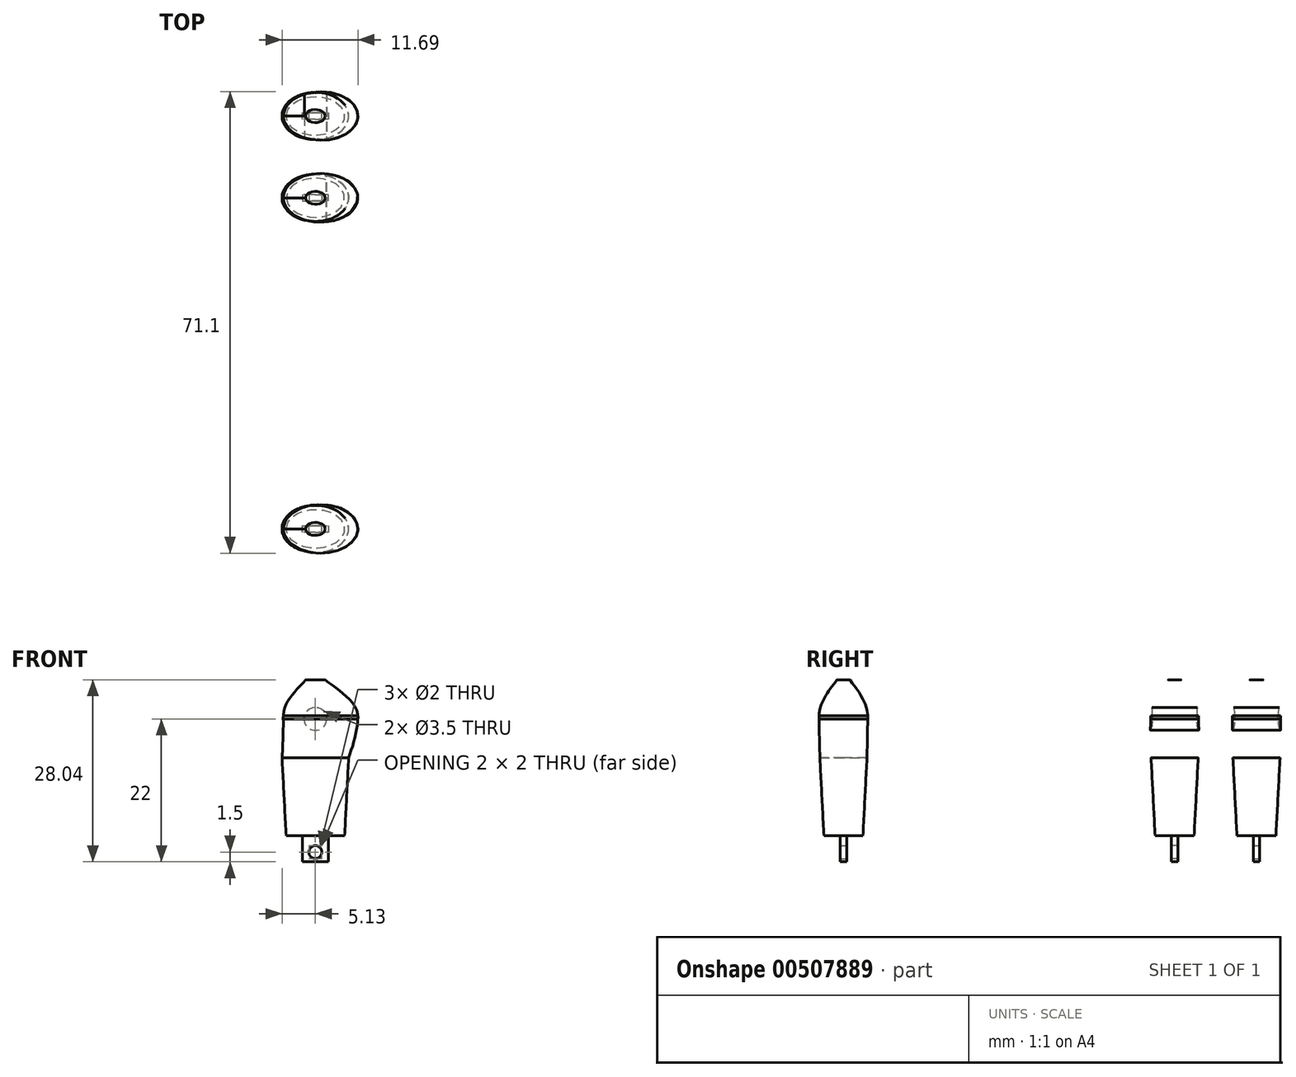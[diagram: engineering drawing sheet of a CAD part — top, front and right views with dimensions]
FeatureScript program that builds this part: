
annotation { "Feature Type Name" : "Feature", "Feature Type Description" : "" }
export const myFeature = defineFeature(function(context is Context, id is Id, definition is map)
    precondition{}
    {
        {
            var Q0;
            Q0=qCreatedBy(makeId("Top.planeOp"),FACE);
            var sketch = newSketch(context, id + "F0", { "sketchPlane" : qUnion([Q0])});
            skEllipse(sketch, "E0", {"center": v(0, 0) * mm, "majorRadius": 4.5 * mm, "minorRadius": 3 * mm, "majorAxis": v(1, 0)});
            skSolve(sketch);
        }
        {
            var Q0;
            Q0=makeQuery(id+"F0.imprint","IMPRINT",FACE,{"disambiguationData":[TD([[makeQuery(id+"F0.imprint","IMPRINT",EDGE,{"derivedFrom":sQuery(id+"F0.wireOp",EDGE,"E0")}),1.0]])]});
            var Q1;
            Q1=sQuery(id+"F0.wireOp",EDGE,"E0");
            extrude(context, id + "F1", {"entities" : qUnion([Q0]), "surfaceEntities" : qUnion([Q1]), "depth" : 12 * mm, "offsetDistance" : 25 * mm, "hasDraft" : true, "draftAngle" : 3 * degree});
        }
        {
            var Q0;
            Q0=makeQuery(id+"F1.opExtrude","CAP_FACE",FACE,{"disambiguationData":[OSD([sQuery(id+"F0.wireOp",EDGE,"E0")])],"isStart":false});
            cPlane(context, id + "F2", {"entities" : qUnion([Q0]), "cplaneType" : CPlaneType.OFFSET, "offset" : 6.5 * mm, "width" : 150 * mm, "height" : 150 * mm});
        }
        {
            var Q0;
            Q0=qCreatedBy(id+"F2.planeOp",FACE);
            var sketch = newSketch(context, id + "F3", { "sketchPlane" : qUnion([Q0])});
            skEllipse(sketch, "E1", {"center": v(0, 0) * mm, "majorRadius": 5.75 * mm, "minorRadius": 3.75 * mm, "majorAxis": v(1, 0)});
            skSolve(sketch);
        }
        {
            var Q0;
            Q0=makeQuery(id+"F3.imprint","IMPRINT",FACE,{"disambiguationData":[TD([[makeQuery(id+"F3.imprint","IMPRINT",EDGE,{"derivedFrom":sQuery(id+"F3.wireOp",EDGE,"E1")}),1.0]])]});
            var Q1;
            Q1=sQuery(id+"F3.wireOp",EDGE,"E1");
            extrude(context, id + "F4", {"entities" : qUnion([Q0]), "surfaceEntities" : qUnion([Q1]), "oppositeDirection" : true, "depth" : .5 * mm, "offsetDistance" : 25 * mm});
        }
        {
            var Q0;
            Q0=makeQuery(id+"F4.opExtrude","SWEPT_BODY",BODY,{"disambiguationData":[OSD([sQuery(id+"F3.wireOp",EDGE,"E1")])]});
            transform(context, id + "F5", {"entities" : qUnion([Q0]), "transformType" : TransformType.TRANSLATION_3D, "dx" : 0.8 * mm, "dy" : 0 * mm, "dz" : 0 * mm, "makeCopy" : false});
        }
        {
            var Q0;
            Q0=makeQuery(id+"F4.opExtrude","CAP_FACE",FACE,{"disambiguationData":[OSD([sQuery(id+"F3.wireOp",EDGE,"E1")])],"isStart":true});
            cPlane(context, id + "F6", {"entities" : qUnion([Q0]), "cplaneType" : CPlaneType.OFFSET, "offset" : 5.5 * mm, "width" : 150 * mm, "height" : 150 * mm});
        }
        {
            var Q0;
            Q0=qCreatedBy(id+"F6.planeOp",FACE);
            var sketch = newSketch(context, id + "F7", { "sketchPlane" : qUnion([Q0])});
            skEllipse(sketch, "E2", {"center": v(0, 0) * mm, "majorRadius": 1.5 * mm, "minorRadius": 1 * mm, "majorAxis": v(1, 0)});
            skSolve(sketch);
        }
        {
            var Q0;
            Q0=makeQuery(id+"F7.imprint","IMPRINT",FACE,{"disambiguationData":[TD([[makeQuery(id+"F7.imprint","IMPRINT",EDGE,{"derivedFrom":sQuery(id+"F7.wireOp",EDGE,"E2")}),1.0]])]});
            var Q1;
            Q1=sQuery(id+"F7.wireOp",EDGE,"E2");
            extrude(context, id + "F8", {"entities" : qUnion([Q0]), "surfaceEntities" : qUnion([Q1]), "depth" : 0.04 * mm, "offsetDistance" : 25 * mm});
        }
        {
            var Q0;
            Q0=makeQuery(id+"F1.opExtrude","CAP_FACE",FACE,{"disambiguationData":[OSD([sQuery(id+"F0.wireOp",EDGE,"E0")])],"isStart":false});
            var Q1;
            Q1=makeQuery(id+"F4.opExtrude","CAP_FACE",FACE,{"disambiguationData":[OSD([sQuery(id+"F3.wireOp",EDGE,"E1")])],"isStart":false});
            var Q2;
            Q2=makeQuery(id+"F4.opExtrude","CAP_FACE",FACE,{"disambiguationData":[OSD([sQuery(id+"F3.wireOp",EDGE,"E1")])],"isStart":true});
            var Q3;
            Q3=makeQuery(id+"F8.opExtrude","CAP_FACE",FACE,{"disambiguationData":[OSD([sQuery(id+"F7.wireOp",EDGE,"E2")])],"isStart":true});
            loft(context, id + "F9", {"sheetProfilesArray" : [{ "sheetProfileEntities" : qUnion([Q0]) }, { "sheetProfileEntities" : qUnion([Q1]) }, { "sheetProfileEntities" : qUnion([Q2]) }, { "sheetProfileEntities" : qUnion([Q3]) }]});
        }
        {
            var Q0;
            Q0=makeQuery(id+"F1.opExtrude","CAP_FACE",FACE,{"disambiguationData":[OSD([sQuery(id+"F0.wireOp",EDGE,"E0")])],"isStart":true});
            var sketch = newSketch(context, id + "F10", { "sketchPlane" : qUnion([Q0])});
            skLineSegment(sketch, "E3", {"start": v(-2, 0) * mm, "end": v(-2, 0.5) * mm});
            skLineSegment(sketch, "E4", {"start": v(-2, 0.5) * mm, "end": v(2, 0.5) * mm});
            skLineSegment(sketch, "E5", {"start": v(2, 0.5) * mm, "end": v(2, 0) * mm});
            skLineSegment(sketch, "E6", {"start": v(2, 0) * mm, "end": v(2, -0.5) * mm});
            skLineSegment(sketch, "E7", {"start": v(2, -0.5) * mm, "end": v(-2, -0.5) * mm});
            skLineSegment(sketch, "E8", {"start": v(-2, -0.5) * mm, "end": v(-2, 0) * mm});
            skLineSegment(sketch, "E9", {"start": v(0, 0) * mm, "end": v(-2, 0) * mm, "construction": true});
            skSolve(sketch);
        }
        {
            var Q0;
            Q0=makeQuery(id+"F10.imprint","IMPRINT",FACE,{"disambiguationData":[TD([[makeQuery(id+"F10.imprint","IMPRINT",EDGE,{"derivedFrom":sQuery(id+"F10.wireOp",EDGE,"E3")}),-1.0]])]});
            extrude(context, id + "F11", {"entities" : qUnion([Q0]), "operationType" : NewBodyOperationType.ADD, "depth" : 4 * mm, "offsetDistance" : 25 * mm});
        }
        {
            var Q0;
            Q0=makeQuery(id+"F11.opExtrude","SWEPT_FACE",FACE,{"disambiguationData":[OSD([sQuery(id+"F10.wireOp",EDGE,"E4")])]});
            var sketch = newSketch(context, id + "F12", { "sketchPlane" : qUnion([Q0])});
            skLineSegment(sketch, "E10", {"start": v(0, 0) * mm, "end": v(0, -2.5) * mm, "construction": true});
            skPoint(sketch, "E10.endSnap0", {"position": v(0, -4) * mm});
            skCircle(sketch, "E11", {"center": v(0, -2.5) * mm, "radius": 1 * mm});
            skSolve(sketch);
        }
        {
            var Q0;
            Q0=makeQuery(id+"F12.imprint","IMPRINT",FACE,{"disambiguationData":[TD([[makeQuery(id+"F12.imprint","IMPRINT",EDGE,{"derivedFrom":sQuery(id+"F12.wireOp",EDGE,"E11")}),1.0]])]});
            var Q1;
            Q1=sQuery(id+"F12.wireOp",EDGE,"E11");
            var Q2;
            Q2=makeQuery(id+"F11.opExtrude","SWEPT_FACE",FACE,{"disambiguationData":[OSD([sQuery(id+"F10.wireOp",EDGE,"E7")])]});
            extrude(context, id + "F13", {"entities" : qUnion([Q0]), "operationType" : NewBodyOperationType.REMOVE, "surfaceEntities" : qUnion([Q1]), "endBound" : BoundingType.UP_TO_SURFACE, "oppositeDirection" : true, "depth" : 2.25 * mm, "endBoundEntityFace" : qUnion([Q2]), "offsetDistance" : 25 * mm});
        }
        {
            var Q0;
            Q0=makeQuery(id+"FBj6Y6sVaxA7N0l_4.opFillet","SPLIT",FACE,{"disambiguationData":[OD(1.0)],"derivedFrom":makeQuery(id+"F11.opExtrude","SWEPT_FACE",FACE,{"disambiguationData":[OSD([sQuery(id+"F10.wireOp",EDGE,"E4")])]})});
            cPlane(context, id + "F14", {"entities" : qUnion([Q0]), "cplaneType" : CPlaneType.OFFSET, "offset" : 25 * mm, "width" : 150 * mm, "height" : 150 * mm});
        }
        {
            var Q0;
            Q0=makeQuery(id+"F1.opExtrude","SWEPT_BODY",BODY,{"disambiguationData":[OSD([sQuery(id+"F0.wireOp",EDGE,"E0")])]});
            var Q1;
            Q1=makeQuery(id+"F8.opExtrude","SWEPT_BODY",BODY,{"disambiguationData":[OSD([sQuery(id+"F7.wireOp",EDGE,"E2")])]});
            var Q2;
            Q2=makeQuery(id+"F4.opExtrude","SWEPT_BODY",BODY,{"disambiguationData":[OSD([sQuery(id+"F3.wireOp",EDGE,"E1")])]});
            var Q3;
            Q3=makeQuery(id+"F9.opLoft","SWEPT_BODY",BODY,{"disambiguationData":[OSD([sQuery(id+"F0.wireOp",EDGE,"E0"),sQuery(id+"F3.wireOp",EDGE,"E1"),sQuery(id+"F7.wireOp",EDGE,"E2")])]});
            var Q4;
            Q4=qCreatedBy(id+"F14.planeOp",FACE);
            mirror(context, id + "F15", {"entities" : qUnion([Q0, Q1, Q2, Q3]), "mirrorPlane" : qUnion([Q4])});
        }
        {
            var Q0;
            Q0=qCreatedBy(makeId("Front.planeOp"),FACE);
            cPlane(context, id + "F16", {"entities" : qUnion([Q0]), "cplaneType" : CPlaneType.OFFSET, "offset" : 6.3 * mm, "oppositeDirection" : true, "width" : 150 * mm, "height" : 150 * mm});
        }
        {
            var Q0;
            Q0=qCreatedBy(id+"F16.planeOp",FACE);
            var sketch = newSketch(context, id + "F17", { "sketchPlane" : qUnion([Q0])});
            skLineSegment(sketch, "E12", {"start": v(0, 0) * mm, "end": v(0, 18) * mm, "construction": true});
            skCircle(sketch, "E13", {"center": v(0, 18) * mm, "radius": 1.75 * mm});
            skSolve(sketch);
        }
        {
            var Q0;
            Q0=makeQuery(id+"F17.imprint","IMPRINT",FACE,{"disambiguationData":[TD([[makeQuery(id+"F17.imprint","IMPRINT",EDGE,{"derivedFrom":sQuery(id+"F17.wireOp",EDGE,"E13")}),1.0]])]});
            var Q1;
            Q1=sQuery(id+"F17.wireOp",EDGE,"E13");
            extrude(context, id + "F18", {"entities" : qUnion([Q0]), "operationType" : NewBodyOperationType.REMOVE, "surfaceEntities" : qUnion([Q1]), "depth" : 12 * mm, "offsetDistance" : 25 * mm});
        }
        {
            var Q0;
            Q0=makeQuery(id+"F9.opLoft","SWEPT_BODY",BODY,{"disambiguationData":[OSD([sQuery(id+"F0.wireOp",EDGE,"E0"),sQuery(id+"F3.wireOp",EDGE,"E1"),sQuery(id+"F7.wireOp",EDGE,"E2")])]});
            var Q1;
            Q1=makeQuery(id+"F4.opExtrude","SWEPT_BODY",BODY,{"disambiguationData":[OSD([sQuery(id+"F3.wireOp",EDGE,"E1")])]});
            var Q2;
            Q2=makeQuery(id+"F8.opExtrude","SWEPT_BODY",BODY,{"disambiguationData":[OSD([sQuery(id+"F7.wireOp",EDGE,"E2")])]});
            var Q3;
            Q3=makeQuery(id+"F1.opExtrude","SWEPT_BODY",BODY,{"disambiguationData":[OSD([sQuery(id+"F0.wireOp",EDGE,"E0")])]});
            var Q4;
            Q4=qCreatedBy(id+"F16.planeOp",FACE);
            mirror(context, id + "F19", {"entities" : qUnion([Q0, Q1, Q2, Q3]), "mirrorPlane" : qUnion([Q4])});
        }
    });
